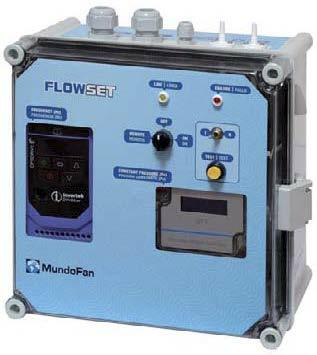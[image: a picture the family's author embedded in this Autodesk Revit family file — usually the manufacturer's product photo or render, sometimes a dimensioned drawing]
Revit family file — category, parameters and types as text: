
# Revit family: FLOWSET-075_VE10842
name_source: partatom
category: Aparatos eléctricos
revit_build: Autodesk Revit 2016 (Build: 20150220_1215(x64)
units: mm (PartAtom-declared; Revit-internal decimal feet)

## family parameters
Compartido = No
Corte con vacíos al cargar = No
Cota de conector redondo = Diámetro de uso
Mantener orientación de anotación = No
Número OmniClass = 23.80.00.00
Punto de cálculo de habitación = No
Se basa en plano de trabajo = No
Siempre vertical = Sí
Tipo de pieza = Caja de conexiones
Título OmniClass = Electric Power and Lighting

## types (1)
- FLOWSET
    Alimentación = 400Vac trifásico
    Corriente = 2,2 A
    Costo = 0 $
    Código de montaje = VE10842
    Descripción = CONTROL EFICIENCIA ENERGETICA PARA VENTILADORES - Caudal aire constante
    Dimensiones máx. = 270x300x170 mm
    Fabricante = SALVADOR ESCODA
    Imagen de tipo = flowset.jpg
    Leds = linea / fallo
    Modelo = FLOWSET 0,75kW
    Normativas = EN-ISO 14644-1:2000
    Potencia = 0,75 kW
    Regulación = Mediante sonda analógica de presión
    Salida = 400Vac trifásico
    Selector = 3 posiciones remoto / off / on
    URL = www.salvadorescoda.com
    Visualización = frecuencia (Hz) y presión (Pa)
